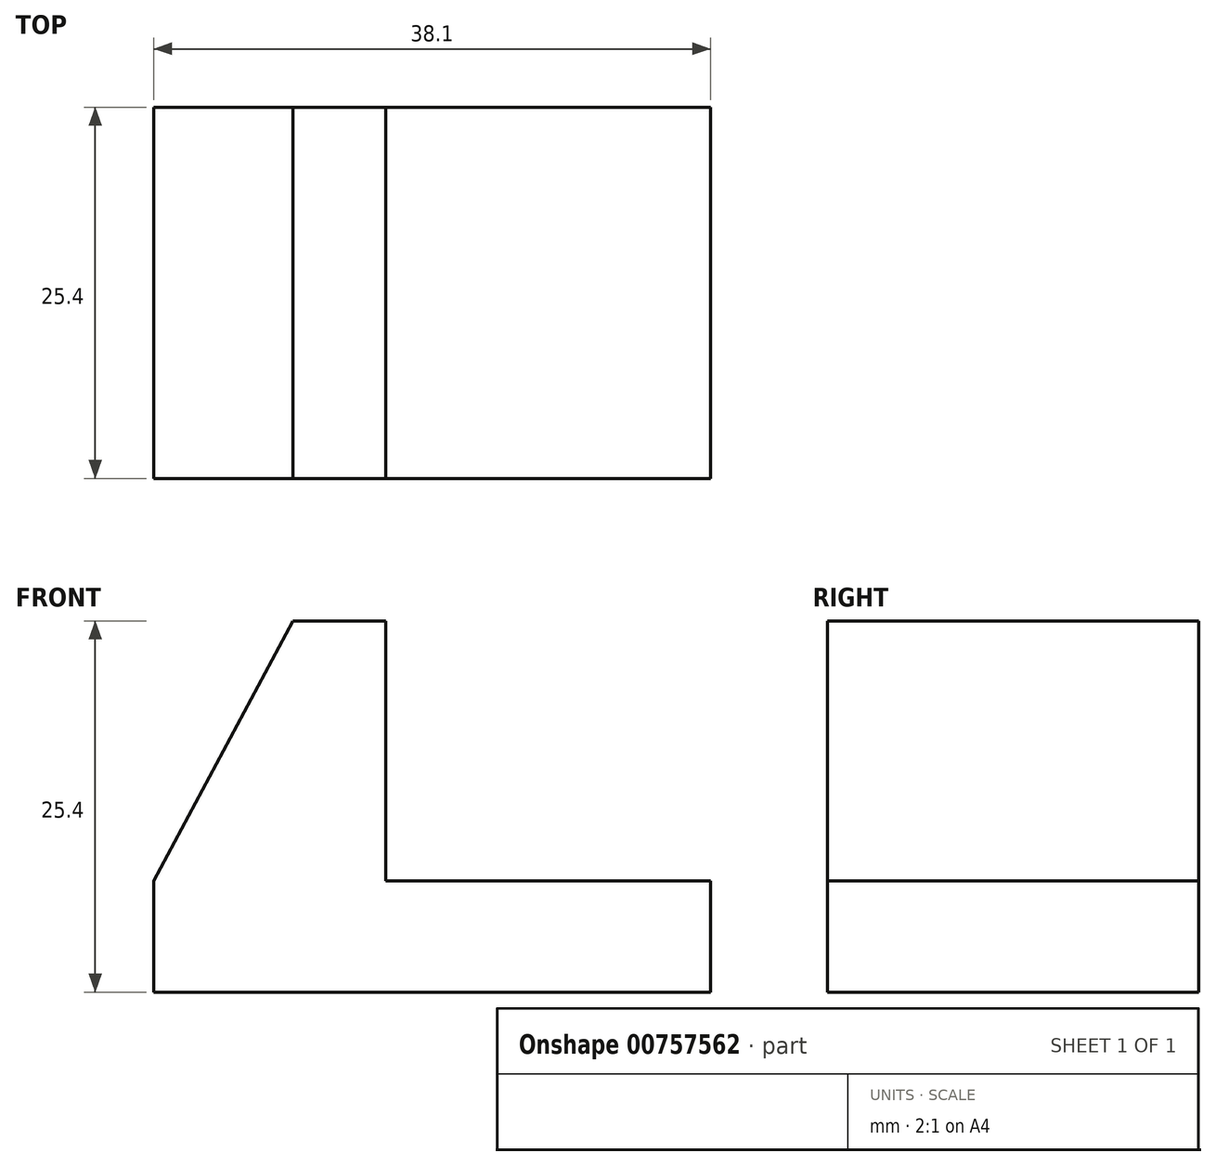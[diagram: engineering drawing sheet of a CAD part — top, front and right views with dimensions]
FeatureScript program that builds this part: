
annotation { "Feature Type Name" : "Feature", "Feature Type Description" : "" }
export const myFeature = defineFeature(function(context is Context, id is Id, definition is map)
    precondition{}
    {
        {
            var Q0;
            Q0=qCreatedBy(makeId("Front.planeOp"),FACE);
            var sketch = newSketch(context, id + "F0", { "sketchPlane" : qUnion([Q0])});
            skArc(sketch, "E0", {"start": v(0, 38.1) * mm, "mid": v(-38.1, 0) * mm, "end": v(0, -38.1) * mm});
            skLineSegment(sketch, "E1", {"start": v(0, -38.1) * mm, "end": v(0, 38.1) * mm, "construction": true});
            skSolve(sketch);
        }
        {
            var Q0;
            Q0 = qSketchRegion(id + "F0", true);
            var Q1;
            Q1=sQuery(id+"F0.wireOp",EDGE,"E0");
            var Q2;
            Q2=sQuery(id+"F0.wireOp",EDGE,"E1");
            revolve(context, id + "F1", {"bodyType" : ToolBodyType.SURFACE, "surfaceOperationType" : NewSurfaceOperationType.NEW, "entities" : qUnion([Q0]), "surfaceEntities" : qUnion([Q1]), "axis" : qUnion([Q2]), "revolveType" : RevolveType.FULL});
        }
        {
            var Q0;
            Q0=qCreatedBy(makeId("Front.planeOp"),FACE);
            var sketch = newSketch(context, id + "F2", { "sketchPlane" : qUnion([Q0])});
            skArc(sketch, "E2", {"start": v(-28.4, 25.4) * mm, "mid": v(-28.63, 25.14) * mm, "end": v(-28.85, 24.88) * mm});
            skLineSegment(sketch, "E3.bottom", {"start": v(-38.1, 0) * mm, "end": v(0, 0) * mm});
            skLineSegment(sketch, "E3.top", {"start": v(-28.58, 25.4) * mm, "end": v(-22.23, 25.4) * mm});
            skLineSegment(sketch, "E3.left", {"start": v(-38.1, 0) * mm, "end": v(-38.1, 7.62) * mm});
            skLineSegment(sketch, "E3.right", {"start": v(0, 0) * mm, "end": v(0, 7.62) * mm});
            skLineSegment(sketch, "E4", {"start": v(-28.58, 25.4) * mm, "end": v(-38.1, 7.62) * mm});
            skLineSegment(sketch, "E5", {"start": v(-22.23, 25.4) * mm, "end": v(-22.23, 7.62) * mm});
            skLineSegment(sketch, "E6", {"start": v(-22.23, 7.62) * mm, "end": v(0, 7.62) * mm});
            skPoint(sketch, "E7.orphan", {"position": v(0, 25.4) * mm});
            skSolve(sketch);
        }
        {
            var Q0;
            Q0 = qSketchRegion(id + "F2", true);
            extrude(context, id + "F3", {"entities" : qUnion([Q0]), "endBound" : BoundingType.SYMMETRIC, "depth" : 25.4 * mm, "offsetDistance" : 25.4 * mm});
        }
    });
